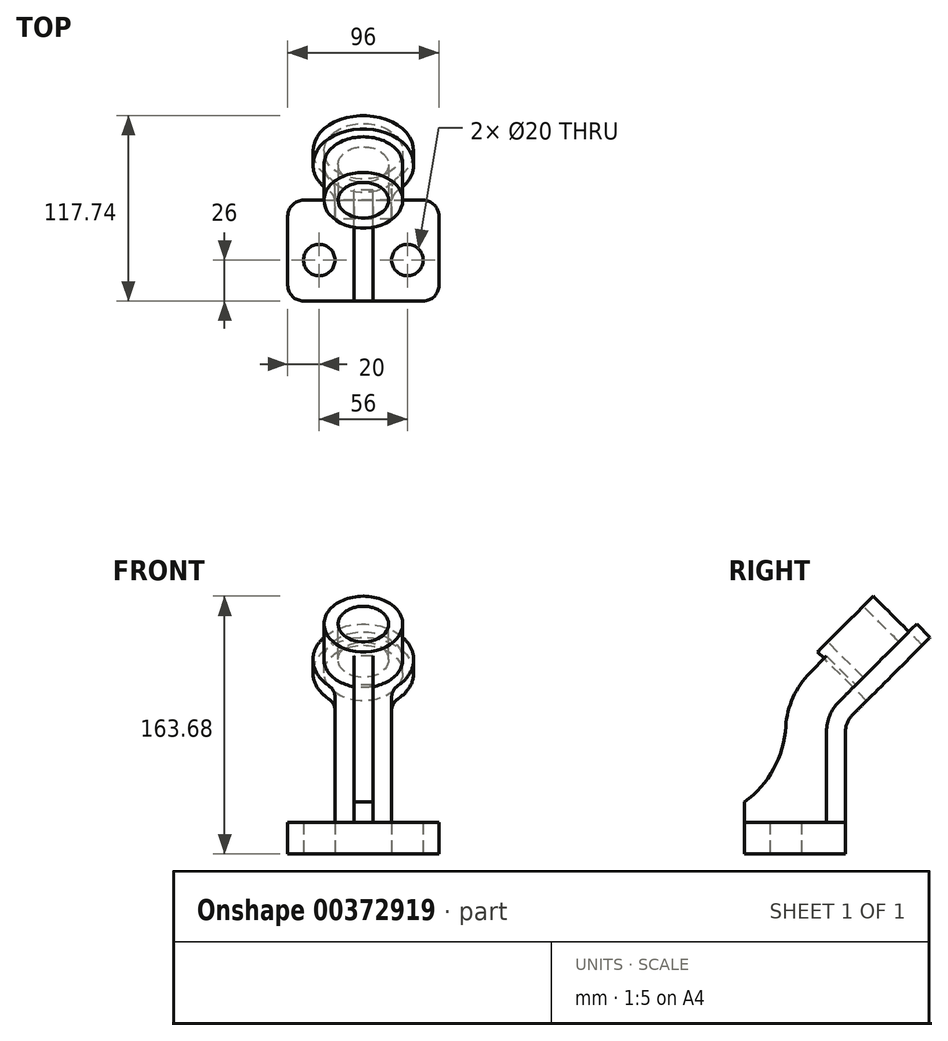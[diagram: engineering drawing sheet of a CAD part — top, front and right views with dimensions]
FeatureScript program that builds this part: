
annotation { "Feature Type Name" : "Feature", "Feature Type Description" : "" }
export const myFeature = defineFeature(function(context is Context, id is Id, definition is map)
    precondition{}
    {
        {
            var Q0;
            Q0=qCreatedBy(makeId("Top.planeOp"),FACE);
            var sketch = newSketch(context, id + "F0", { "sketchPlane" : qUnion([Q0])});
            skLineSegment(sketch, "E0.bottom", {"start": v(-38, 0) * mm, "end": v(38, 0) * mm});
            skLineSegment(sketch, "E0.top", {"start": v(-38, 64) * mm, "end": v(38, 64) * mm});
            skLineSegment(sketch, "E0.left", {"start": v(-48, 10) * mm, "end": v(-48, 54) * mm});
            skLineSegment(sketch, "E0.right", {"start": v(48, 10) * mm, "end": v(48, 54) * mm});
            skCircle(sketch, "E1", {"center": v(-28, 26) * mm, "radius": 10 * mm});
            skCircle(sketch, "E2.MirrorC", {"center": v(28, 26) * mm, "radius": 10 * mm});
            skPoint(sketch, "E3.visualSharp", {"position": v(-48, 64) * mm});
            skArc(sketch, "E3.filletArc", {"start": v(-38, 64) * mm, "mid": v(-45.07, 61.07) * mm, "end": v(-48, 54) * mm});
            skPoint(sketch, "E4.visualSharp", {"position": v(-48, 0) * mm});
            skArc(sketch, "E4.filletArc", {"start": v(-48, 10) * mm, "mid": v(-45.07, 2.93) * mm, "end": v(-38, 0) * mm});
            skPoint(sketch, "E5.visualSharp", {"position": v(48, 0) * mm});
            skArc(sketch, "E5.filletArc", {"start": v(38, 0) * mm, "mid": v(45.07, 2.93) * mm, "end": v(48, 10) * mm});
            skPoint(sketch, "E6.visualSharp", {"position": v(48, 64) * mm});
            skArc(sketch, "E6.filletArc", {"start": v(48, 54) * mm, "mid": v(45.07, 61.07) * mm, "end": v(38, 64) * mm});
            skSolve(sketch);
        }
        {
            var Q0;
            Q0=makeQuery(id+"F0.imprint","IMPRINT",FACE,{"disambiguationData":[TD([[makeQuery(id+"F0.imprint","IMPRINT",EDGE,{"derivedFrom":sQuery(id+"F0.wireOp",EDGE,"E0.bottom")}),1.0]])]});
            extrude(context, id + "F1", {"entities" : qUnion([Q0]), "depth" : 20 * mm});
        }
        {
            var Q0;
            Q0=qCreatedBy(makeId("Right.planeOp"),FACE);
            var sketch = newSketch(context, id + "F2", { "sketchPlane" : qUnion([Q0])});
            skLineSegment(sketch, "E7", {"start": v(64, 146) * mm, "end": v(166.26, 248.26) * mm});
            skSolve(sketch);
        }
        {
            var Q0;
            Q0=sQuery(id+"F2.wireOp",EDGE,"E7");
            extrude(context, id + "F3", {"bodyType" : ToolBodyType.SURFACE, "surfaceEntities" : qUnion([Q0]), "depth" : 25 * mm, "hasSecondDirection" : true, "secondDirectionOppositeDirection" : true, "secondDirectionDepth" : 25 * mm});
        }
        {
            var Q0;
            Q0=makeQuery(id+"F3.opExtrude","SWEPT_FACE",FACE,{"disambiguationData":[OSD([sQuery(id+"F2.wireOp",EDGE,"E7")])]});
            var sketch = newSketch(context, id + "F4", { "sketchPlane" : qUnion([Q0])});
            skCircle(sketch, "E8", {"center": v(0, 148.5) * mm, "radius": 16 * mm});
            skCircle(sketch, "E9", {"center": v(0, 148.5) * mm, "radius": 25 * mm});
            skSolve(sketch);
        }
        {
            var Q0;
            {var subQ0=sQuery(id+"F4.wireOp",EDGE,"E8");var subQ1=makeQuery(id+"F3.opExtrude","SWEPT_EDGE",EDGE,{"disambiguationData":[OSD([sQuery(id+"F2.wireOp",VERTEX,"E7.start")])]});var subQ2=makeQuery(id+"F4.imprint","INTERSECT",VERTEX,{"disambiguationData":[OD(0.0)],"derivedFrom":[subQ1,subQ0]});Q0=makeQuery(id+"F4.imprint","IMPRINT",FACE,{"disambiguationData":[TD([[makeQuery(id+"F4.imprint","IMPRINT",EDGE,{"disambiguationData":[TD([[subQ2,1.0]])],"derivedFrom":subQ0}),-1.0]])]});}
            var Q1;
            {var subQ0=sQuery(id+"F4.wireOp",EDGE,"E8");var subQ1=makeQuery(id+"F3.opExtrude","SWEPT_EDGE",EDGE,{"disambiguationData":[OSD([sQuery(id+"F2.wireOp",VERTEX,"E7.start")])]});var subQ2=makeQuery(id+"F4.imprint","INTERSECT",VERTEX,{"disambiguationData":[OD(0.0)],"derivedFrom":[subQ1,subQ0]});Q1=makeQuery(id+"F4.imprint","IMPRINT",FACE,{"disambiguationData":[TD([[makeQuery(id+"F4.imprint","IMPRINT",EDGE,{"disambiguationData":[TD([[subQ2,-1.0]])],"derivedFrom":subQ0}),-1.0]])]});}
            extrude(context, id + "F5", {"entities" : qUnion([Q0, Q1]), "depth" : 32 * mm});
        }
        {
            var Q0;
            Q0=makeQuery(id+"F5.opExtrude","CAP_FACE",FACE,{"disambiguationData":[OSD([sQuery(id+"F4.wireOp",EDGE,"E8"),sQuery(id+"F4.wireOp",EDGE,"E9")])],"isStart":false});
            var sketch = newSketch(context, id + "F6", { "sketchPlane" : qUnion([Q0])});
            skCircle(sketch, "E10", {"center": v(0, 148.5) * mm, "radius": 32 * mm});
            skSolve(sketch);
        }
        {
            var Q0;
            Q0=makeQuery(id+"F6.imprint","IMPRINT",FACE,{"disambiguationData":[TD([[makeQuery(id+"F6.imprint","IMPRINT",EDGE,{"derivedFrom":sQuery(id+"F6.wireOp",EDGE,"E10")}),1.0]])]});
            extrude(context, id + "F7", {"entities" : qUnion([Q0]), "depth" : 12 * mm});
        }
        {
            var Q0;
            Q0=qCreatedBy(makeId("Right.planeOp"),FACE);
            var sketch = newSketch(context, id + "F8", { "sketchPlane" : qUnion([Q0])});
            skLineSegment(sketch, "E11.0", {"start": v(64, 20) * mm, "end": v(64, 0) * mm});
            skLineSegment(sketch, "E12.0", {"start": v(0, 20) * mm, "end": v(0, 0) * mm});
            skLineSegment(sketch, "E13", {"start": v(64, 20) * mm, "end": v(64, 77.56) * mm});
            skArc(sketch, "E14.filletArc", {"start": v(68.4, 88.17) * mm, "mid": v(65.14, 83.3) * mm, "end": v(64, 77.56) * mm});
            skLineSegment(sketch, "E15.0", {"start": v(52, 20) * mm, "end": v(52, 77.56) * mm});
            skArc(sketch, "E16.0", {"start": v(59.9, 96.65) * mm, "mid": v(54.06, 87.9) * mm, "end": v(52, 77.56) * mm});
            skLineSegment(sketch, "E17", {"start": v(52, 20) * mm, "end": v(64, 20) * mm});
            skLineSegment(sketch, "E18", {"start": v(68.4, 88.17) * mm, "end": v(76.47, 96.25) * mm});
            skLineSegment(sketch, "E19.0", {"start": v(59.9, 96.65) * mm, "end": v(67.99, 104.73) * mm});
            skLineSegment(sketch, "E20", {"start": v(67.99, 104.73) * mm, "end": v(76.47, 96.25) * mm});
            skSolve(sketch);
        }
        {
            var Q0;
            Q0=makeQuery(id+"F8.imprint","IMPRINT",FACE,{"disambiguationData":[TD([[makeQuery(id+"F8.imprint","IMPRINT",EDGE,{"derivedFrom":sQuery(id+"F8.wireOp",EDGE,"E13")}),1.0]])]});
            extrude(context, id + "F9", {"entities" : qUnion([Q0]), "depth" : 18 * mm, "hasSecondDirection" : true, "secondDirectionOppositeDirection" : true, "secondDirectionDepth" : 18 * mm});
        }
        {
            var Q0;
            Q0=makeQuery(id+"F9.opExtrude","SWEPT_BODY",BODY,{"disambiguationData":[OSD([sQuery(id+"F8.wireOp",EDGE,"E13"),sQuery(id+"F8.wireOp",EDGE,"E14.filletArc"),sQuery(id+"F8.wireOp",EDGE,"E15.0"),sQuery(id+"F8.wireOp",EDGE,"E16.0"),sQuery(id+"F8.wireOp",EDGE,"E17"),sQuery(id+"F8.wireOp",EDGE,"E18"),sQuery(id+"F8.wireOp",EDGE,"E19.0"),sQuery(id+"F8.wireOp",EDGE,"E20")])]});
            var Q1;
            Q1=makeQuery(id+"F7.opExtrude","SWEPT_BODY",BODY,{"disambiguationData":[OSD([sQuery(id+"F4.wireOp",EDGE,"E9"),sQuery(id+"F6.wireOp",EDGE,"E10")])]});
            booleanBodies(context, id + "F10", {"operationType" : BooleanOperationType.UNION, "tools" : qUnion([Q0, Q1])});
        }
        {
            var Q0;
            Q0=makeQuery(id+"F10.opBoolean","INTERSECT",EDGE,{"derivedFrom":[makeQuery(id+"F7.opExtrude","SWEPT_FACE",FACE,{"disambiguationData":[OSD([sQuery(id+"F6.wireOp",EDGE,"E10")])]}),makeQuery(id+"F9.opExtrude","CAP_FACE",FACE,{"disambiguationData":[OSD([sQuery(id+"F8.wireOp",EDGE,"E13"),sQuery(id+"F8.wireOp",EDGE,"E14.filletArc"),sQuery(id+"F8.wireOp",EDGE,"E15.0"),sQuery(id+"F8.wireOp",EDGE,"E16.0"),sQuery(id+"F8.wireOp",EDGE,"E17"),sQuery(id+"F8.wireOp",EDGE,"E18"),sQuery(id+"F8.wireOp",EDGE,"E19.0"),sQuery(id+"F8.wireOp",EDGE,"E20")])],"isStart":false})]});
            var Q1;
            Q1=makeQuery(id+"F10.opBoolean","INTERSECT",EDGE,{"derivedFrom":[makeQuery(id+"F7.opExtrude","SWEPT_FACE",FACE,{"disambiguationData":[OSD([sQuery(id+"F6.wireOp",EDGE,"E10")])]}),makeQuery(id+"F9.opExtrude","CAP_FACE",FACE,{"disambiguationData":[OSD([sQuery(id+"F8.wireOp",EDGE,"E13"),sQuery(id+"F8.wireOp",EDGE,"E14.filletArc"),sQuery(id+"F8.wireOp",EDGE,"E15.0"),sQuery(id+"F8.wireOp",EDGE,"E16.0"),sQuery(id+"F8.wireOp",EDGE,"E17"),sQuery(id+"F8.wireOp",EDGE,"E18"),sQuery(id+"F8.wireOp",EDGE,"E19.0"),sQuery(id+"F8.wireOp",EDGE,"E20")])],"isStart":true})]});
            fillet(context, id + "F11", {"entities" : qUnion([Q0, Q1]), "radius" : 15 * mm, "tangentPropagation" : true, "allowEdgeOverflow" : false});
        }
        {
            var Q0;
            Q0=qCreatedBy(makeId("Right.planeOp"),FACE);
            var sketch = newSketch(context, id + "F12", { "sketchPlane" : qUnion([Q0])});
            skArc(sketch, "E21.0", {"start": v(41.52, 115.04) * mm, "mid": v(30.7, 99.4) * mm, "end": v(26.1, 80.94) * mm});
            skLineSegment(sketch, "E22.0", {"start": v(62.96, 99.7) * mm, "end": v(70.52, 107.26) * mm});
            skArc(sketch, "E23.0", {"start": v(59.9, 96.65) * mm, "mid": v(54.06, 87.9) * mm, "end": v(52, 77.56) * mm});
            skLineSegment(sketch, "E24.0", {"start": v(0, 20) * mm, "end": v(0, 0) * mm});
            skLineSegment(sketch, "E25", {"start": v(0, 20) * mm, "end": v(0, 32.86) * mm});
            skPoint(sketch, "E26.third.point", {"position": v(-103.79, 80.94) * mm});
            skLineSegment(sketch, "E27.0", {"start": v(10, 20) * mm, "end": v(54, 20) * mm});
            skLineSegment(sketch, "E28.0", {"start": v(52, 20) * mm, "end": v(52, 77.56) * mm});
            skLineSegment(sketch, "E29", {"start": v(0, 20) * mm, "end": v(10, 20) * mm});
            skLineSegment(sketch, "E30", {"start": v(59.9, 96.65) * mm, "end": v(62.96, 99.7) * mm});
            skLineSegment(sketch, "E31", {"start": v(41.52, 115.04) * mm, "end": v(52.06, 125.57) * mm});
            skLineSegment(sketch, "E32", {"start": v(52.06, 125.57) * mm, "end": v(70.52, 107.26) * mm});
            skArc(sketch, "E33", {"start": v(-38.84, 20) * mm, "mid": v(5.69, 37.62) * mm, "end": v(26.1, 80.94) * mm});
            skLineSegment(sketch, "E34", {"start": v(0, 20) * mm, "end": v(-38.84, 20) * mm});
            skSolve(sketch);
        }
        {
            var Q0;
            Q0=makeQuery(id+"F12.imprint","IMPRINT",FACE,{"disambiguationData":[TD([[makeQuery(id+"F12.imprint","IMPRINT",EDGE,{"derivedFrom":sQuery(id+"F12.wireOp",EDGE,"E21.0")}),1.0]])]});
            extrude(context, id + "F13", {"entities" : qUnion([Q0]), "depth" : 6 * mm, "hasSecondDirection" : true, "secondDirectionOppositeDirection" : true, "secondDirectionDepth" : 6 * mm});
        }
    });
